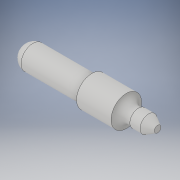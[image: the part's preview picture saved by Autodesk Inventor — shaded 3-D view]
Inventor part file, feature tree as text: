
AUTODESK INVENTOR PART (.ipt)
format: ipt  version: 2018.3 (Build 223284000, 284)  size: 147,968 bytes
history: native  units: in
note: dims shown in document units (in); Inventor stores cm internally (conversion verified against a paired STEP export)
features: sketch x2, revolve x1
ambient origin geometry x8: Origin, YZ Plane, XZ Plane, XY Plane, X Axis, Y Axis, Z Axis, Center Point
bodies: Body1 (feature_tree)
feature tree (3):
  sketch  "Sketch1"  dims[d0=0.025in d1=0.0645in]
  sketch  "Sketch2"  dims[d3=0.47in d4=0.115in d6=0.13in d8=0.222in d11=0.03in d13=0.025in d14=0.0645in d15=0.115in d19=90.0deg]
  revolve  "Revolution1"  [1 undecoded]
note: 1 required parameter value undecoded (feature->parameter linkage not recoverable at this tier; creation-order binding heuristic only, values carry confidence <= 0.55)
